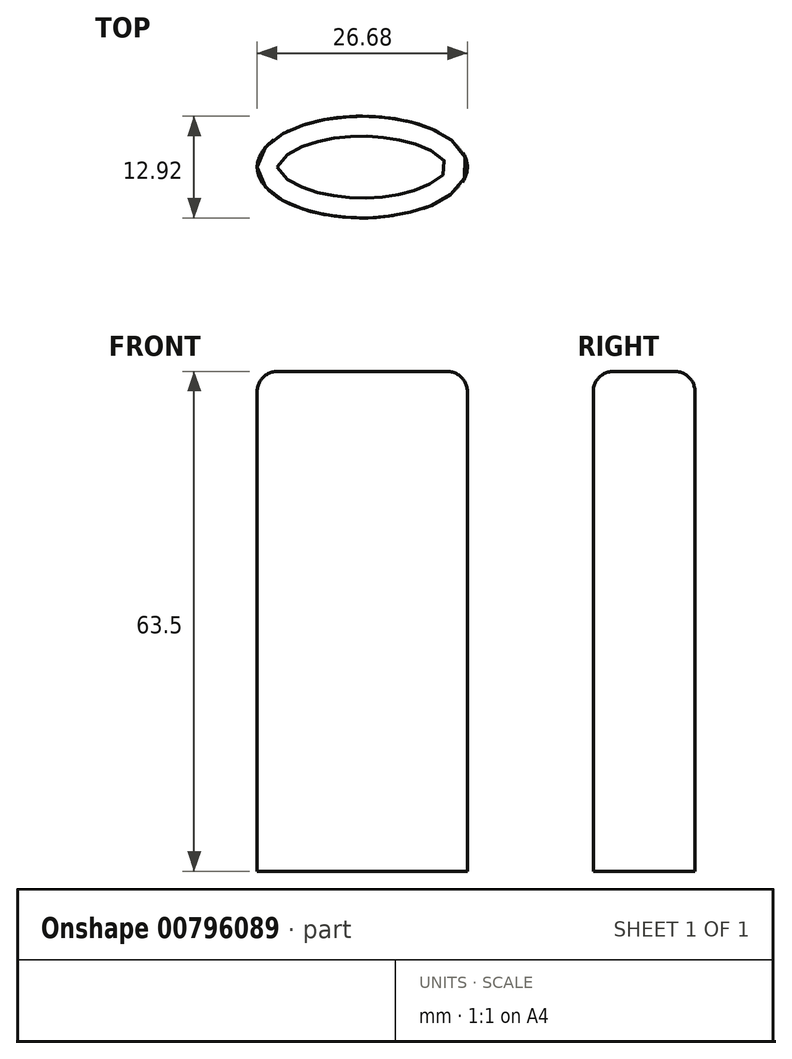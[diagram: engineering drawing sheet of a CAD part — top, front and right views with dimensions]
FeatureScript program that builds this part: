
annotation { "Feature Type Name" : "Feature", "Feature Type Description" : "" }
export const myFeature = defineFeature(function(context is Context, id is Id, definition is map)
    precondition{}
    {
        {
            var Q0;
            Q0=qCreatedBy(makeId("Top.planeOp"),FACE);
            var sketch = newSketch(context, id + "F0", { "sketchPlane" : qUnion([Q0])});
            skEllipse(sketch, "E0", {"center": v(0, 0) * mm, "majorRadius": 13.34 * mm, "minorRadius": 6.46 * mm, "majorAxis": v(-1, 0)});
            skSolve(sketch);
        }
        {
            var Q0;
            Q0 = qSketchRegion(id + "F0", true);
            extrude(context, id + "F1", {"entities" : qUnion([Q0]), "depth" : 63.5 * mm, "offsetDistance" : 25.4 * mm});
        }
        {
            var Q0;
            Q0=makeQuery(id+"F1.opExtrude","CAP_FACE",FACE,{"disambiguationData":[OSD([sQuery(id+"F0.wireOp",EDGE,"E0")])],"isStart":false});
            fillet(context, id + "F2", {"entities" : qUnion([Q0]), "radius" : 2.54 * mm, "tangentPropagation" : true, "allowEdgeOverflow" : false});
        }
    });
